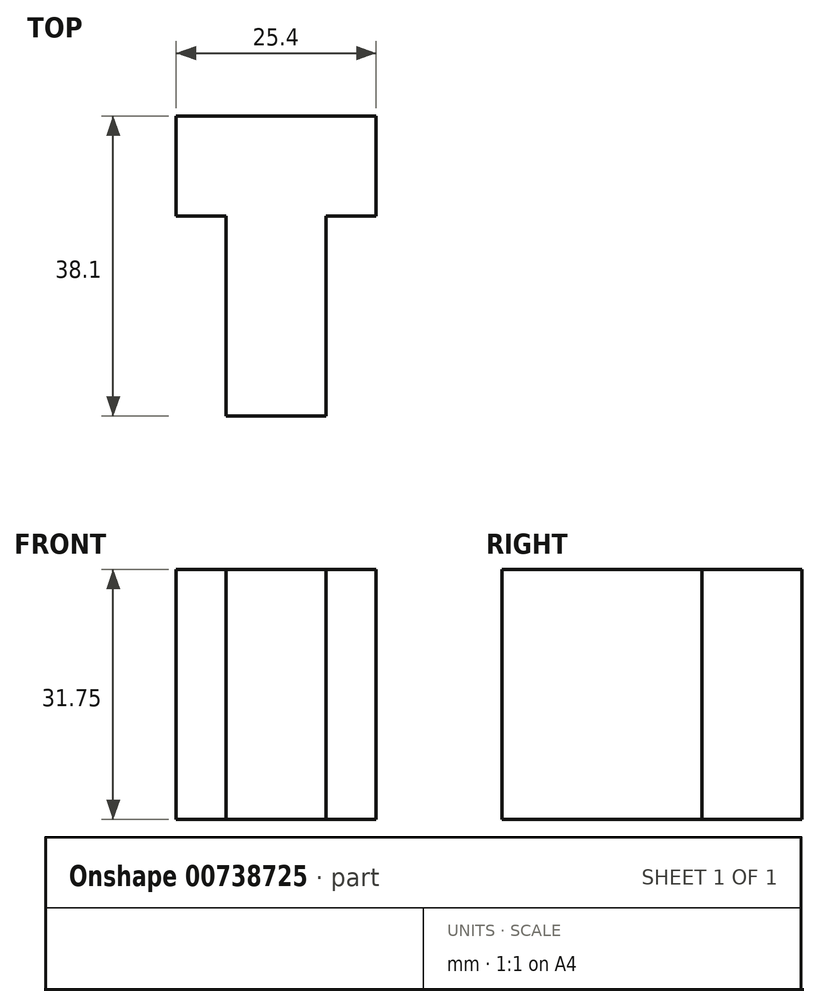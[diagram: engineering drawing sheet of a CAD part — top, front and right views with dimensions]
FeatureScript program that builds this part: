
annotation { "Feature Type Name" : "Feature", "Feature Type Description" : "" }
export const myFeature = defineFeature(function(context is Context, id is Id, definition is map)
    precondition{}
    {
        {
            var Q0;
            Q0=qCreatedBy(makeId("Top.planeOp"),FACE);
            var sketch = newSketch(context, id + "F0", { "sketchPlane" : qUnion([Q0])});
            skLineSegment(sketch, "E0", {"start": v(0, 0) * mm, "end": v(-12.7, 0) * mm});
            skLineSegment(sketch, "E1", {"start": v(-12.7, 0) * mm, "end": v(-12.7, 25.4) * mm});
            skLineSegment(sketch, "E2", {"start": v(-12.7, 25.4) * mm, "end": v(-19.05, 25.4) * mm});
            skLineSegment(sketch, "E3", {"start": v(-19.05, 25.4) * mm, "end": v(-19.05, 38.1) * mm});
            skLineSegment(sketch, "E4", {"start": v(-19.05, 38.1) * mm, "end": v(6.35, 38.1) * mm});
            skLineSegment(sketch, "E5", {"start": v(6.35, 38.1) * mm, "end": v(6.35, 25.4) * mm});
            skLineSegment(sketch, "E6", {"start": v(6.35, 25.4) * mm, "end": v(0, 25.4) * mm});
            skLineSegment(sketch, "E7", {"start": v(0, 25.4) * mm, "end": v(0, 0) * mm});
            skSolve(sketch);
        }
        {
            var Q0;
            Q0 = qSketchRegion(id + "F0", true);
            extrude(context, id + "F1", {"entities" : qUnion([Q0]), "depth" : 31.75 * mm, "offsetDistance" : 25.4 * mm});
        }
    });
